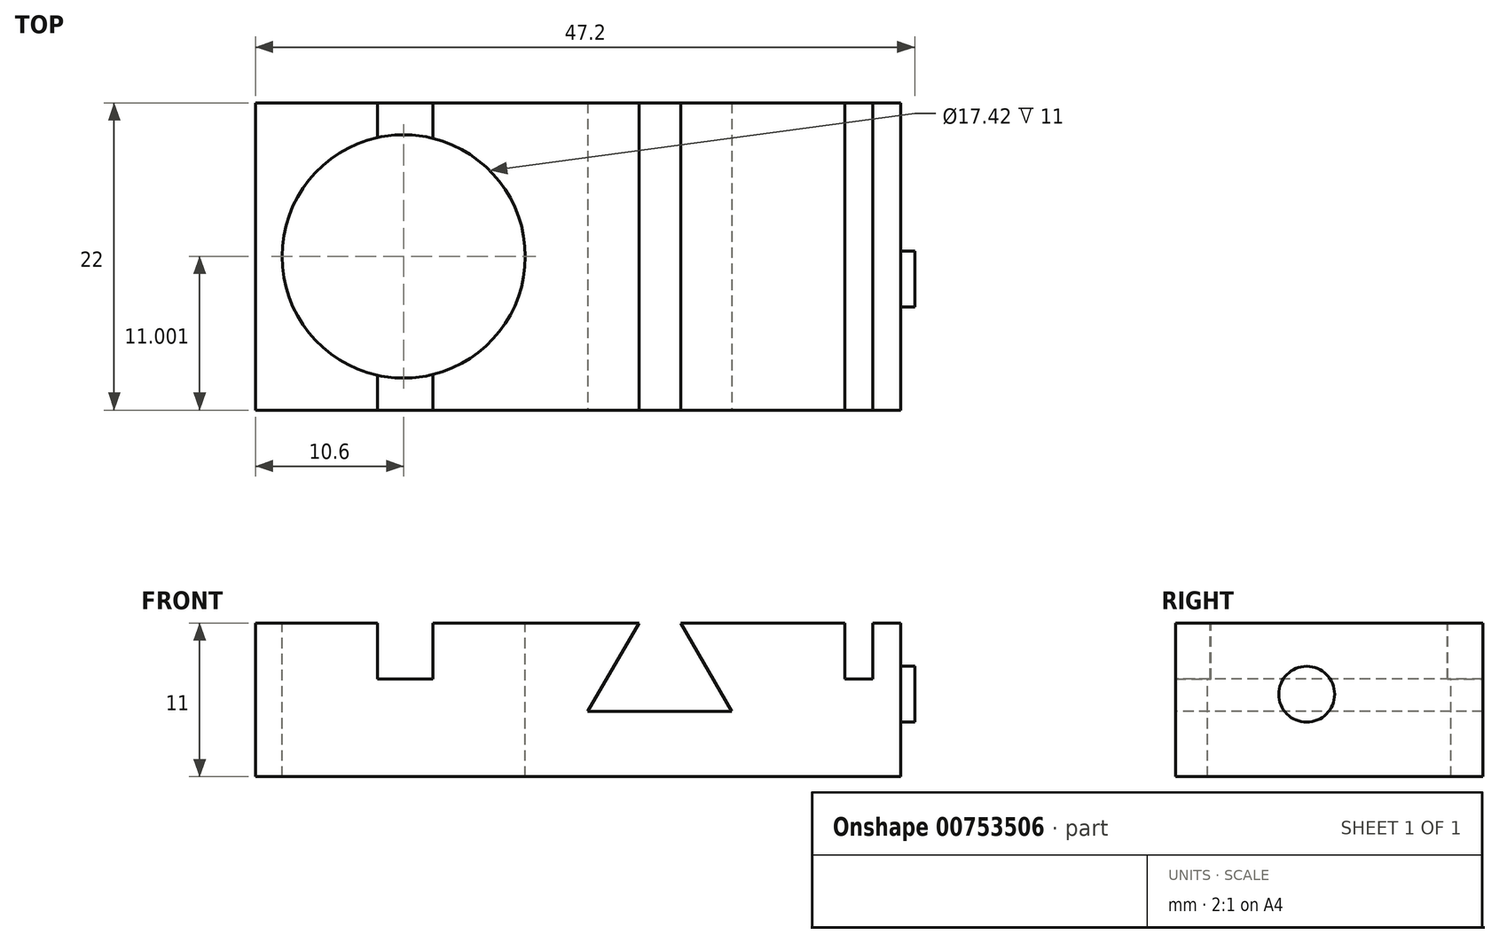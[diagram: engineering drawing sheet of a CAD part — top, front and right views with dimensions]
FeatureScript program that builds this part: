
annotation { "Feature Type Name" : "Feature", "Feature Type Description" : "" }
export const myFeature = defineFeature(function(context is Context, id is Id, definition is map)
    precondition{}
    {
        {
            var Q0;
            Q0=qCreatedBy(makeId("Top.planeOp"),FACE);
            var sketch = newSketch(context, id + "F0", { "sketchPlane" : qUnion([Q0])});
            skLineSegment(sketch, "E0.bottom", {"start": v(10.6, 10.54) * mm, "end": v(-10.6, 10.54) * mm});
            skLineSegment(sketch, "E0.top", {"start": v(10.6, -11.46) * mm, "end": v(-10.6, -11.46) * mm});
            skLineSegment(sketch, "E0.left", {"start": v(10.6, 10.54) * mm, "end": v(10.6, -11.46) * mm});
            skLineSegment(sketch, "E0.right", {"start": v(-10.6, 10.54) * mm, "end": v(-10.6, -11.46) * mm});
            skPoint(sketch, "E0.middle", {"position": v(0, -0.46) * mm});
            skCircle(sketch, "E1", {"center": v(0, -0.46) * mm, "radius": 8.71 * mm});
            skSolve(sketch);
        }
        {
            var Q0;
            Q0=makeQuery(id+"F0.imprint","IMPRINT",FACE,{"disambiguationData":[TD([[makeQuery(id+"F0.imprint","IMPRINT",EDGE,{"derivedFrom":sQuery(id+"F0.wireOp",EDGE,"E0.bottom")}),1.0]])]});
            extrude(context, id + "F1", {"entities" : qUnion([Q0]), "oppositeDirection" : true, "depth" : 11 * mm, "offsetDistance" : 25.4 * mm});
        }
        {
            var Q0;
            Q0=makeQuery(id+"F1.opExtrude","SWEPT_FACE",FACE,{"disambiguationData":[OSD([sQuery(id+"F0.wireOp",EDGE,"E0.left")])]});
            extrude(context, id + "F2", {"entities" : qUnion([Q0]), "operationType" : NewBodyOperationType.ADD, "depth" : 25 * mm, "offsetDistance" : 25 * mm});
        }
        {
            var Q0;
            {var subQ0=sQuery(id+"F0.wireOp",EDGE,"E0.left");Q0=makeQuery(id+"F2.boolean.opBoolean","MERGE",FACE,{"derivedFrom":[makeQuery(id+"F1.opExtrude","CAP_FACE",FACE,{"disambiguationData":[OSD([sQuery(id+"F0.wireOp",EDGE,"E0.bottom"),sQuery(id+"F0.wireOp",EDGE,"E0.top"),subQ0,sQuery(id+"F0.wireOp",EDGE,"E0.right"),sQuery(id+"F0.wireOp",EDGE,"E1")])],"isStart":true}),makeQuery(id+"F2.opExtrude","SWEPT_FACE",FACE,{"disambiguationData":[OSD([subQ0]),TDD([makeQuery(id+"F1.opExtrude","CAP_EDGE",EDGE,{"disambiguationData":[OSD([subQ0])],"isStart":true})])]})]});}
            var sketch = newSketch(context, id + "F3", { "sketchPlane" : qUnion([Q0])});
            skLineSegment(sketch, "E2.bottom", {"start": v(31.6, 10.54) * mm, "end": v(33.6, 10.54) * mm});
            skLineSegment(sketch, "E2.top", {"start": v(31.6, -11.46) * mm, "end": v(33.6, -11.46) * mm});
            skLineSegment(sketch, "E2.left", {"start": v(31.6, 10.54) * mm, "end": v(31.6, -11.46) * mm});
            skLineSegment(sketch, "E2.right", {"start": v(33.6, 10.54) * mm, "end": v(33.6, -11.46) * mm});
            skLineSegment(sketch, "E3", {"start": v(2.1, 10.54) * mm, "end": v(2.1, -11.46) * mm});
            skLineSegment(sketch, "E4", {"start": v(2.1, -11.46) * mm, "end": v(-1.86, -11.46) * mm});
            skLineSegment(sketch, "E5", {"start": v(-1.86, -11.46) * mm, "end": v(-1.86, 10.54) * mm});
            skPoint(sketch, "E6", {"position": v(-3.1, 0) * mm});
            skPoint(sketch, "E7", {"position": v(0, 0) * mm});
            skLineSegment(sketch, "E8", {"start": v(0.12, -11.46) * mm, "end": v(2.1, 10.54) * mm, "construction": true});
            skSolve(sketch);
        }
        {
            var Q0;
            Q0=makeQuery(id+"F3.imprint","IMPRINT",FACE,{"disambiguationData":[TD([[makeQuery(id+"F3.imprint","IMPRINT",EDGE,{"derivedFrom":sQuery(id+"F3.wireOp",EDGE,"E2.bottom")}),1.0]])]});
            var Q1;
            {var subQ0=sQuery(id+"F3.wireOp",EDGE,"E4");Q1=makeQuery(id+"F3.imprint","IMPRINT",FACE,{"disambiguationData":[TD([[makeQuery(id+"F3.imprint","IMPRINT",EDGE,{"derivedFrom":subQ0}),-1.0]])]});}
            var Q2;
            {var subQ0=sQuery(id+"F3.wireOp",EDGE,"E3");var subQ5=makeQuery(id+"F1.opExtrude","CAP_EDGE",EDGE,{"disambiguationData":[OSD([sQuery(id+"F0.wireOp",EDGE,"E1")])],"isStart":true});var subQ6=makeQuery(id+"F3.imprint","INTERSECT",VERTEX,{"disambiguationData":[OD(0.0)],"derivedFrom":[subQ5,subQ0]});Q2=makeQuery(id+"F3.imprint","IMPRINT",FACE,{"disambiguationData":[TD([[makeQuery(id+"F3.imprint","IMPRINT",EDGE,{"disambiguationData":[TD([[subQ6,-1.0]])],"derivedFrom":subQ5}),-1.0]])]});}
            extrude(context, id + "F4", {"entities" : qUnion([Q0, Q1, Q2]), "operationType" : NewBodyOperationType.REMOVE, "oppositeDirection" : true, "depth" : 4 * mm, "offsetDistance" : 25 * mm});
        }
        {
            var Q0;
            {var subQ0=sQuery(id+"F0.wireOp",EDGE,"E0.top");Q0=makeQuery(id+"F2.boolean.opBoolean","MERGE",FACE,{"derivedFrom":[makeQuery(id+"F1.opExtrude","SWEPT_FACE",FACE,{"disambiguationData":[OSD([subQ0])]}),makeQuery(id+"F2.opExtrude","SWEPT_FACE",FACE,{"disambiguationData":[OSD([subQ0,sQuery(id+"F0.wireOp",EDGE,"E0.left")])]})]});}
            var sketch = newSketch(context, id + "F5", { "sketchPlane" : qUnion([Q0])});
            skLineSegment(sketch, "E9", {"start": v(16.85, 0) * mm, "end": v(13.2, -6.33) * mm});
            skLineSegment(sketch, "E10", {"start": v(13.2, -6.33) * mm, "end": v(23.5, -6.33) * mm});
            skLineSegment(sketch, "E11", {"start": v(23.5, -6.33) * mm, "end": v(19.85, 0) * mm});
            skLineSegment(sketch, "E12", {"start": v(19.85, 0) * mm, "end": v(16.85, 0) * mm});
            skLineSegment(sketch, "E13", {"start": v(18.35, -6.33) * mm, "end": v(18.35, 0) * mm, "construction": true});
            skSolve(sketch);
        }
        {
            var Q0;
            Q0 = qSketchRegion(id + "F5", true);
            extrude(context, id + "F6", {"entities" : qUnion([Q0]), "operationType" : NewBodyOperationType.REMOVE, "endBound" : BoundingType.THROUGH_ALL, "oppositeDirection" : true, "depth" : 7 * mm, "offsetDistance" : 25 * mm});
        }
        {
            var Q0;
            Q0=makeQuery(id+"F2.opExtrude","CAP_FACE",FACE,{"disambiguationData":[OSD([sQuery(id+"F0.wireOp",EDGE,"E0.left")])],"isStart":false});
            var sketch = newSketch(context, id + "F7", { "sketchPlane" : qUnion([Q0])});
            skCircle(sketch, "E14", {"center": v(-2.06, -5.1) * mm, "radius": 2 * mm});
            skSolve(sketch);
        }
        {
            var Q0;
            Q0=makeQuery(id+"F7.imprint","IMPRINT",FACE,{"disambiguationData":[TD([[makeQuery(id+"F7.imprint","IMPRINT",EDGE,{"derivedFrom":sQuery(id+"F7.wireOp",EDGE,"E14")}),1.0]])]});
            extrude(context, id + "F8", {"entities" : qUnion([Q0]), "operationType" : NewBodyOperationType.ADD, "depth" : 1 * mm, "offsetDistance" : 25 * mm});
        }
    });
